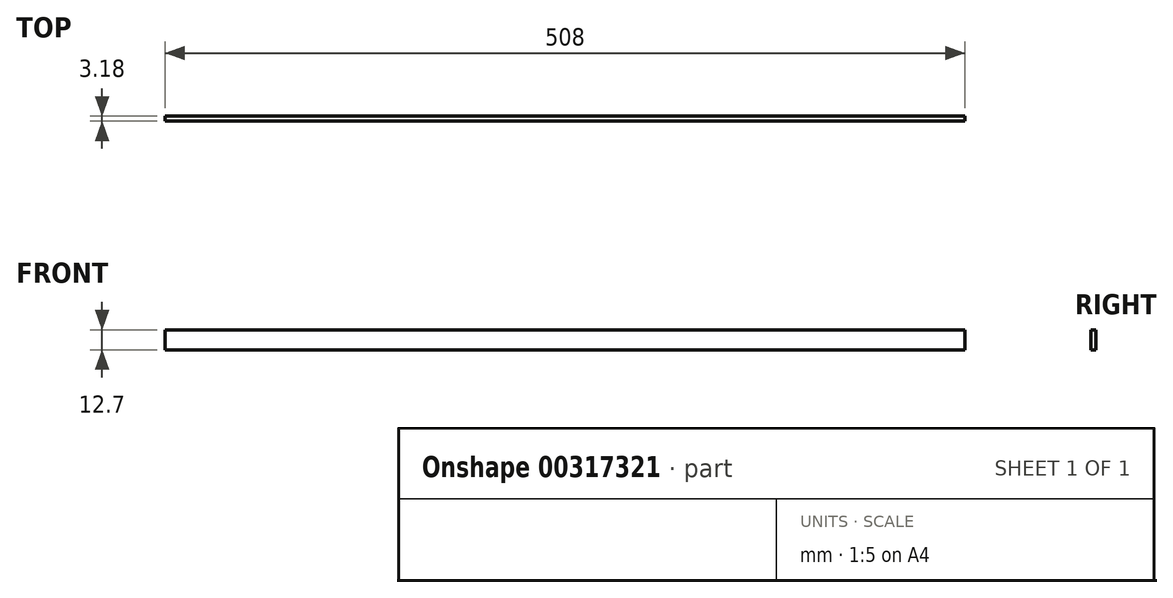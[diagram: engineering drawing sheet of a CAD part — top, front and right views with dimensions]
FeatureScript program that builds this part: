
annotation { "Feature Type Name" : "Feature", "Feature Type Description" : "" }
export const myFeature = defineFeature(function(context is Context, id is Id, definition is map)
    precondition{}
    {
        {
            var Q0;
            Q0=qCreatedBy(makeId("Front.planeOp"),FACE);
            var sketch = newSketch(context, id + "F0", { "sketchPlane" : qUnion([Q0])});
            skLineSegment(sketch, "E0.bottom", {"start": v(254, 6.35) * mm, "end": v(-254, 6.35) * mm});
            skLineSegment(sketch, "E0.top", {"start": v(254, -6.35) * mm, "end": v(-254, -6.35) * mm});
            skLineSegment(sketch, "E0.left", {"start": v(254, 6.35) * mm, "end": v(254, -6.35) * mm});
            skLineSegment(sketch, "E0.right", {"start": v(-254, 6.35) * mm, "end": v(-254, -6.35) * mm});
            skPoint(sketch, "E0.middle", {"position": v(0, 0) * mm});
            skSolve(sketch);
        }
        {
            var Q0;
            Q0=makeQuery(id+"F0.imprint","IMPRINT",FACE,{"disambiguationData":[TD([[makeQuery(id+"F0.imprint","IMPRINT",EDGE,{"derivedFrom":sQuery(id+"F0.wireOp",EDGE,"E0.bottom")}),1.0]])]});
            extrude(context, id + "F1", {"entities" : qUnion([Q0]), "endBound" : BoundingType.SYMMETRIC, "depth" : 3.17 * mm});
        }
    });
